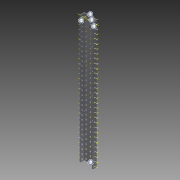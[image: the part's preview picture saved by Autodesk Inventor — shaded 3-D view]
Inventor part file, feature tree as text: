
AUTODESK INVENTOR PART (.ipt)
format: ipt  version: 2015 SP1 (Build 190203100, 203)  size: 2,274,816 bytes
history: native  units: in
note: dims shown in document units (in); Inventor stores cm internally (conversion verified against a paired STEP export)
features: other x156, pattern_linear x2, sheet_metal_op x1, extrude x1, imported_body x1, sketch x1
ambient origin geometry x8: Origin, YZ Plane, XZ Plane, XY Plane, X Axis, Y Axis, Z Axis, Center Point
bodies: Body1 (feature_tree)
feature tree (162):
  sheet_metal_op  "Fold1"
  other  "C-Channel"
  extrude  "length cut"  Depth=1.1811in
  other  "Work Point1"
  other  "Work Point2"
  other  "Work Point3"
  other  "top axis"
  other  "front axis"
  other  "back axis"
  pattern_linear  "top axes"  Count1=30  [1 undecoded]
  pattern_linear  "horiz axes"  Spacing1=0.5in  [1 undecoded]
  other  "Left Plane"
  other  "Right Plane"
  imported_body  "Base1"
  sketch  "Sketch1"  dims[d1=0.0in d2=1.1811in d4=0.5in d5=11.811in d7=0.5in d8=11.811in d10=0.5in d12=-15.0in d17=0.0in d18=0.0in d19=0.0in d20=0.0in d21=0.0in]
  other  "Work Axis4"
  other  "Work Axis5"
  other  "Work Axis6"
  other  "Work Axis7"
  other  "Work Axis8"
  other  "Work Axis9"
  other  "Work Axis10"
  other  "Work Axis11"
  other  "Work Axis12"
  other  "Work Axis13"
  other  "Work Axis14"
  other  "Work Axis15"
  other  "Work Axis16"
  other  "Work Axis17"
  other  "Work Axis18"
  other  "Work Axis19"
  other  "Work Axis20"
  other  "Work Axis21"
  other  "Work Axis22"
  other  "Work Axis23"
  other  "Work Axis24"
  other  "Work Axis25"
  other  "Work Axis26"
  other  "Work Axis27"
  other  "Work Axis28"
  other  "Work Axis29"
  other  "Work Axis30"
  other  "Work Axis31"
  other  "Work Axis32"
  other  "Work Axis33"
  other  "Work Axis34"
  other  "Work Axis35"
  other  "Work Axis36"
  other  "Work Axis37"
  other  "Work Axis38"
  other  "Work Axis39"
  other  "Work Axis40"
  other  "Work Axis41"
  other  "Work Axis42"
  other  "Work Axis43"
  other  "Work Axis44"
  other  "Work Axis45"
  other  "Work Axis46"
  other  "Work Axis47"
  other  "Work Axis48"
  other  "Work Axis49"
  other  "Work Axis50"
  other  "Work Axis51"
  other  "Work Axis52"
  other  "Work Axis53"
  other  "Work Axis54"
  other  "Work Axis55"
  other  "Work Axis56"
  other  "Work Axis57"
  other  "Work Axis58"
  other  "Work Axis59"
  other  "Work Axis60"
  other  "Work Axis61"
  other  "Work Axis62"
  other  "Work Axis63"
  other  "Work Axis64"
  other  "Work Axis65"
  other  "Work Axis66"
  other  "Work Axis67"
  other  "Work Axis68"
  other  "Work Axis69"
  other  "Work Axis70"
  other  "Work Axis71"
  other  "Work Axis72"
  other  "Work Axis73"
  other  "Work Axis74"
  other  "Work Axis75"
  other  "Work Axis76"
  other  "Work Axis77"
  other  "Work Axis78"
  other  "Work Axis79"
  other  "Work Axis80"
  other  "Work Axis81"
  other  "Work Axis82"
  other  "Work Axis83"
  other  "Work Axis84"
  other  "Work Axis85"
  other  "Work Axis86"
  other  "Work Axis87"
  other  "Work Axis88"
  other  "Work Axis89"
  other  "Work Axis90"
  other  "Work Axis91"
  other  "Work Axis92"
  other  "Work Axis93"
  other  "Work Axis94"
  other  "Work Axis95"
  other  "Work Axis96"
  other  "Work Axis97"
  other  "Work Axis98"
  other  "Work Axis99"
  other  "Work Axis100"
  other  "Work Axis101"
  other  "Work Axis102"
  other  "Work Axis103"
  other  "Work Axis104"
  other  "Work Axis105"
  other  "Work Axis106"
  other  "Work Axis107"
  other  "Work Axis108"
  other  "Work Axis109"
  other  "Work Axis110"
  other  "Work Axis111"
  other  "Work Axis112"
  other  "Work Axis113"
  other  "Work Axis114"
  other  "Work Axis115"
  other  "Work Axis116"
  other  "Work Axis117"
  other  "Work Axis118"
  other  "Work Axis119"
  other  "Work Axis120"
  other  "Work Axis121"
  other  "Work Axis122"
  other  "Work Axis123"
  other  "Work Axis124"
  other  "Work Axis125"
  other  "Work Axis151"
  other  "Work Axis152"
  other  "Work Axis153"
  other  "Work Axis154"
  other  "Work Axis155"
  other  "Work Axis156"
  other  "Work Axis157"
  other  "Work Axis158"
  other  "Work Axis159"
  other  "Work Axis160"
  other  "Work Axis161"
  other  "Work Axis162"
  other  "Work Axis163"
  other  "Work Axis164"
  other  "Work Axis165"
  other  "Work Axis166"
  other  "Work Axis167"
  other  "Work Axis168"
  other  "Work Axis169"
  other  "Work Axis170"
  other  "Work Axis171"
  other  "Work Axis172"
  other  "Work Axis173"
  other  "Work Axis174"
  other  "Work Axis175"
note: 2 required parameter values undecoded (feature->parameter linkage not recoverable at this tier; creation-order binding heuristic only, values carry confidence <= 0.55)
